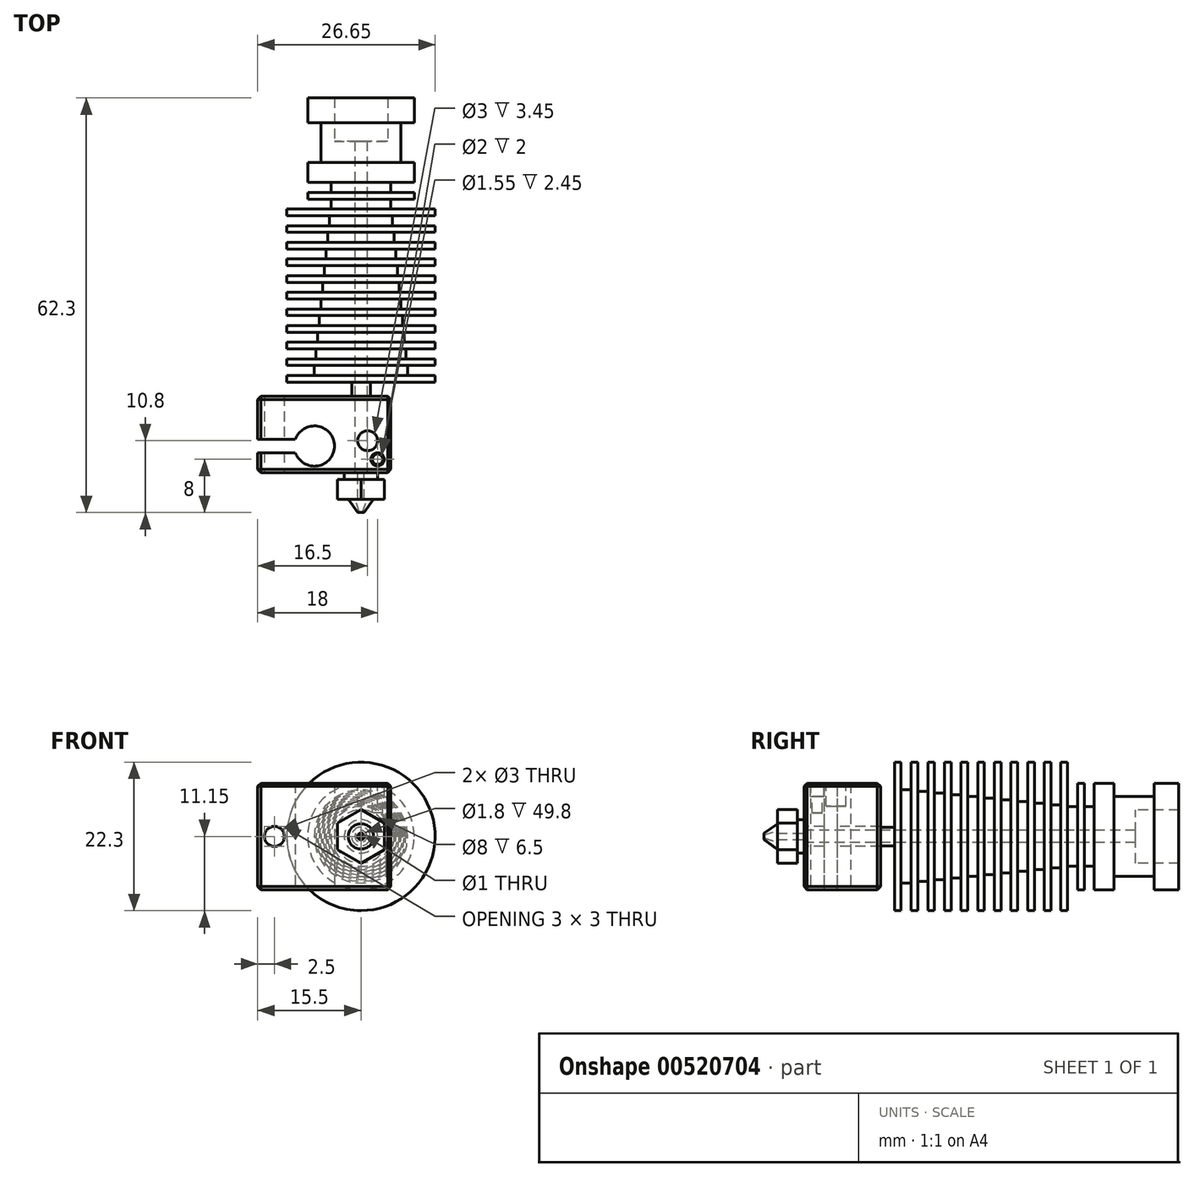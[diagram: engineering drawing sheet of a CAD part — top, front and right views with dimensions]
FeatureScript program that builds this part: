
annotation { "Feature Type Name" : "Feature", "Feature Type Description" : "" }
export const myFeature = defineFeature(function(context is Context, id is Id, definition is map)
    precondition{}
    {
        {
            var Q0;
            Q0=qCreatedBy(makeId("Top.planeOp"),FACE);
            var sketch = newSketch(context, id + "F0", { "sketchPlane" : qUnion([Q0])});
            skLineSegment(sketch, "E0", {"start": v(-8, 21.35) * mm, "end": v(-0.9, 21.35) * mm, "construction": true});
            skLineSegment(sketch, "E1", {"start": v(-0.9, 21.35) * mm, "end": v(-0.9, -38.95) * mm});
            skLineSegment(sketch, "E2", {"start": v(-0.9, 21.35) * mm, "end": v(-8, 21.35) * mm});
            skLineSegment(sketch, "E3", {"start": v(-6, 17.65) * mm, "end": v(-6, 11.65) * mm});
            skLineSegment(sketch, "E4", {"start": v(-8, 17.65) * mm, "end": v(-6, 17.65) * mm});
            skLineSegment(sketch, "E5", {"start": v(-8, 17.65) * mm, "end": v(-8, 21.35) * mm});
            skLineSegment(sketch, "E6", {"start": v(-8, 11.65) * mm, "end": v(-6, 11.65) * mm});
            skLineSegment(sketch, "E7", {"start": v(-8, 11.65) * mm, "end": v(-8, 8.65) * mm});
            skLineSegment(sketch, "E8", {"start": v(-8, 8.65) * mm, "end": v(-4.5, 8.65) * mm});
            skLineSegment(sketch, "E9", {"start": v(-4.5, 8.65) * mm, "end": v(-4.5, 7.15) * mm});
            skLineSegment(sketch, "E10", {"start": v(-4.5, 7.15) * mm, "end": v(-8, 7.15) * mm});
            skLineSegment(sketch, "E11", {"start": v(-8, 7.15) * mm, "end": v(-8, 6.15) * mm});
            skLineSegment(sketch, "E12", {"start": v(-8, 6.15) * mm, "end": v(-4.5, 6.15) * mm});
            skLineSegment(sketch, "E13", {"start": v(-4.5, 6.15) * mm, "end": v(-4.5, 4.65) * mm});
            skLineSegment(sketch, "E14", {"start": v(-4.5, 4.65) * mm, "end": v(-11.15, 4.65) * mm});
            skLineSegment(sketch, "E15", {"start": v(-11.15, 4.65) * mm, "end": v(-11.15, 3.65) * mm});
            skLineSegment(sketch, "E16", {"start": v(-11.15, 3.65) * mm, "end": v(-4.75, 3.65) * mm});
            skLineSegment(sketch, "E17", {"start": v(-4.75, 3.65) * mm, "end": v(-4.75, 2.15) * mm});
            skLineSegment(sketch, "E18", {"start": v(-4.75, 2.15) * mm, "end": v(-11.15, 2.15) * mm});
            skLineSegment(sketch, "E19", {"start": v(-11.15, 2.15) * mm, "end": v(-11.15, 1.15) * mm});
            skLineSegment(sketch, "E20", {"start": v(-11.15, 1.15) * mm, "end": v(-5, 1.15) * mm});
            skLineSegment(sketch, "E21", {"start": v(-5, 1.15) * mm, "end": v(-5, -0.35) * mm});
            skLineSegment(sketch, "E22", {"start": v(-5, -0.35) * mm, "end": v(-11.15, -0.35) * mm});
            skLineSegment(sketch, "E23", {"start": v(-11.15, -0.35) * mm, "end": v(-11.15, -1.35) * mm});
            skLineSegment(sketch, "E24", {"start": v(-11.15, -1.35) * mm, "end": v(-5.25, -1.35) * mm});
            skLineSegment(sketch, "E25", {"start": v(-5.25, -1.35) * mm, "end": v(-5.25, -2.85) * mm});
            skLineSegment(sketch, "E26", {"start": v(-5.25, -2.85) * mm, "end": v(-11.15, -2.85) * mm});
            skLineSegment(sketch, "E27", {"start": v(-11.15, -2.85) * mm, "end": v(-11.15, -3.85) * mm});
            skLineSegment(sketch, "E28", {"start": v(-11.15, -3.85) * mm, "end": v(-5.5, -3.85) * mm});
            skLineSegment(sketch, "E29", {"start": v(-5.5, -3.85) * mm, "end": v(-5.5, -5.35) * mm});
            skLineSegment(sketch, "E30", {"start": v(-5.5, -5.35) * mm, "end": v(-11.15, -5.35) * mm});
            skLineSegment(sketch, "E31", {"start": v(-11.15, -5.35) * mm, "end": v(-11.15, -6.35) * mm});
            skLineSegment(sketch, "E32", {"start": v(-11.15, -6.35) * mm, "end": v(-5.75, -6.35) * mm});
            skLineSegment(sketch, "E33", {"start": v(-5.75, -6.35) * mm, "end": v(-5.75, -7.85) * mm});
            skLineSegment(sketch, "E34", {"start": v(-5.75, -7.85) * mm, "end": v(-11.15, -7.85) * mm});
            skLineSegment(sketch, "E35", {"start": v(-11.15, -7.85) * mm, "end": v(-11.15, -8.85) * mm});
            skLineSegment(sketch, "E36", {"start": v(-11.15, -8.85) * mm, "end": v(-6, -8.85) * mm});
            skLineSegment(sketch, "E37", {"start": v(-6, -8.85) * mm, "end": v(-6, -10.35) * mm});
            skLineSegment(sketch, "E38", {"start": v(-6, -10.35) * mm, "end": v(-11.15, -10.35) * mm});
            skLineSegment(sketch, "E39", {"start": v(-11.15, -10.35) * mm, "end": v(-11.15, -11.35) * mm});
            skLineSegment(sketch, "E40", {"start": v(-11.15, -11.35) * mm, "end": v(-6.25, -11.35) * mm});
            skLineSegment(sketch, "E41", {"start": v(-6.25, -11.35) * mm, "end": v(-6.25, -12.85) * mm});
            skLineSegment(sketch, "E42", {"start": v(-6.25, -12.85) * mm, "end": v(-11.15, -12.85) * mm});
            skLineSegment(sketch, "E43", {"start": v(-11.15, -12.85) * mm, "end": v(-11.15, -13.85) * mm});
            skLineSegment(sketch, "E44", {"start": v(-11.15, -13.85) * mm, "end": v(-6.5, -13.85) * mm});
            skLineSegment(sketch, "E45", {"start": v(-6.5, -13.85) * mm, "end": v(-6.5, -15.35) * mm});
            skLineSegment(sketch, "E46", {"start": v(-6.5, -15.35) * mm, "end": v(-11.15, -15.35) * mm});
            skLineSegment(sketch, "E47", {"start": v(-11.15, -15.35) * mm, "end": v(-11.15, -16.35) * mm});
            skLineSegment(sketch, "E48", {"start": v(-11.15, -16.35) * mm, "end": v(-6.75, -16.35) * mm});
            skLineSegment(sketch, "E49", {"start": v(-6.75, -16.35) * mm, "end": v(-6.75, -17.85) * mm});
            skLineSegment(sketch, "E50", {"start": v(-6.75, -17.85) * mm, "end": v(-11.15, -17.85) * mm});
            skLineSegment(sketch, "E51", {"start": v(-11.15, -17.85) * mm, "end": v(-11.15, -18.85) * mm});
            skLineSegment(sketch, "E52", {"start": v(-11.15, -18.85) * mm, "end": v(-7, -18.85) * mm});
            skLineSegment(sketch, "E53", {"start": v(-7, -18.85) * mm, "end": v(-7, -20.35) * mm});
            skLineSegment(sketch, "E54", {"start": v(-7, -20.35) * mm, "end": v(-11.15, -20.35) * mm});
            skLineSegment(sketch, "E55", {"start": v(-11.15, -20.35) * mm, "end": v(-11.15, -21.35) * mm});
            skLineSegment(sketch, "E56", {"start": v(-11.15, -21.35) * mm, "end": v(-1.4, -21.35) * mm});
            skLineSegment(sketch, "E57", {"start": v(-1.4, -21.35) * mm, "end": v(-1.4, -23.45) * mm});
            skLineSegment(sketch, "E58", {"start": v(-1.4, -23.45) * mm, "end": v(-1.4, -34.95) * mm});
            skLineSegment(sketch, "E59", {"start": v(-1.4, -34.95) * mm, "end": v(-2.5, -34.95) * mm});
            skLineSegment(sketch, "E60", {"start": v(-2.5, -34.95) * mm, "end": v(-2.5, -35.95) * mm});
            skLineSegment(sketch, "E61", {"start": v(-0.2, -40.95) * mm, "end": v(-0.9, -38.95) * mm});
            skLineSegment(sketch, "E62", {"start": v(-0.2, -40.95) * mm, "end": v(-0.5, -40.95) * mm});
            skLineSegment(sketch, "E63", {"start": v(-0.5, -40.95) * mm, "end": v(-1.9, -38.95) * mm});
            skLineSegment(sketch, "E64", {"start": v(-1.9, -38.95) * mm, "end": v(-2.5, -35.95) * mm});
            skLineSegment(sketch, "E65", {"start": v(0, 0) * mm, "end": v(0, 30) * mm, "construction": true});
            skLineSegment(sketch, "E66", {"start": v(-1.4, -23.45) * mm, "end": v(-15.5, -23.45) * mm});
            skLineSegment(sketch, "E67", {"start": v(-15.5, -23.45) * mm, "end": v(-15.5, -34.95) * mm});
            skLineSegment(sketch, "E68", {"start": v(-15.5, -34.95) * mm, "end": v(4.5, -34.95) * mm});
            skLineSegment(sketch, "E69", {"start": v(4.5, -34.95) * mm, "end": v(4.5, -23.45) * mm});
            skLineSegment(sketch, "E70", {"start": v(4.5, -23.45) * mm, "end": v(-1.4, -23.45) * mm});
            skLineSegment(sketch, "E71", {"start": v(-15.5, -29.95) * mm, "end": v(-9.85, -29.95) * mm});
            skLineSegment(sketch, "E72", {"start": v(-15.5, -31.95) * mm, "end": v(-9.85, -31.95) * mm});
            skArc(sketch, "E73", {"start": v(-9.85, -31.95) * mm, "mid": v(-3.97, -30.95) * mm, "end": v(-9.85, -29.95) * mm});
            skLineSegment(sketch, "E74", {"start": v(0, -23.45) * mm, "end": v(0, -34.95) * mm});
            skLineSegment(sketch, "E75", {"start": v(-4, 21.35) * mm, "end": v(-4, 14.85) * mm});
            skLineSegment(sketch, "E76", {"start": v(-4, 14.85) * mm, "end": v(-0.9, 14.85) * mm});
            skSolve(sketch);
        }
        {
            var Q0;
            {var subQ6=sQuery(id+"F0.wireOp",EDGE,"E58");Q0=makeQuery(id+"F0.imprint","IMPRINT",FACE,{"disambiguationData":[TD([[makeQuery(id+"F0.imprint","IMPRINT",EDGE,{"derivedFrom":subQ6}),-1.0]])]});}
            var Q1;
            {var subQ5=sQuery(id+"F0.wireOp",EDGE,"E69");Q1=makeQuery(id+"F0.imprint","IMPRINT",FACE,{"disambiguationData":[TD([[makeQuery(id+"F0.imprint","IMPRINT",EDGE,{"derivedFrom":subQ5}),1.0]])]});}
            var Q2;
            {var subQ5=sQuery(id+"F0.wireOp",EDGE,"E58");Q2=makeQuery(id+"F0.imprint","IMPRINT",FACE,{"disambiguationData":[TD([[makeQuery(id+"F0.imprint","IMPRINT",EDGE,{"derivedFrom":subQ5}),1.0]])]});}
            var Q3;
            {var subQ5=sQuery(id+"F0.wireOp",EDGE,"E74");Q3=makeQuery(id+"F0.imprint","IMPRINT",FACE,{"disambiguationData":[TD([[makeQuery(id+"F0.imprint","IMPRINT",EDGE,{"derivedFrom":subQ5}),-1.0]])]});}
            extrude(context, id + "F1", {"entities" : qUnion([Q0, Q1, Q2, Q3]), "depth" : 8 * mm, "offsetDistance" : 25 * mm, "hasSecondDirection" : true, "secondDirectionOppositeDirection" : true, "secondDirectionDepth" : 8 * mm});
        }
        {
            var Q0;
            {var subQ5=sQuery(id+"F0.wireOp",EDGE,"E58");Q0=makeQuery(id+"F0.imprint","IMPRINT",FACE,{"disambiguationData":[TD([[makeQuery(id+"F0.imprint","IMPRINT",EDGE,{"derivedFrom":subQ5}),1.0]])]});}
            var Q1;
            {var subQ0=sQuery(id+"F0.wireOp",EDGE,"E60");Q1=makeQuery(id+"F0.imprint","IMPRINT",FACE,{"disambiguationData":[TD([[makeQuery(id+"F0.imprint","IMPRINT",EDGE,{"derivedFrom":subQ0}),1.0]])]});}
            var Q2;
            Q2=makeQuery(id+"F0.imprint","IMPRINT",FACE,{"disambiguationData":[TD([[makeQuery(id+"F0.imprint","IMPRINT",EDGE,{"derivedFrom":sQuery(id+"F0.wireOp",EDGE,"E3")}),1.0]])]});
            var Q3;
            Q3=sQuery(id+"F0.wireOp",EDGE,"E65");
            revolve(context, id + "F2", {"operationType" : NewBodyOperationType.ADD, "entities" : qUnion([Q0, Q1, Q2]), "axis" : qUnion([Q3]), "revolveType" : RevolveType.FULL});
        }
        {
            var Q0;
            {var subQ5=sQuery(id+"F0.wireOp",EDGE,"E74");Q0=makeQuery(id+"F0.imprint","IMPRINT",FACE,{"disambiguationData":[TD([[makeQuery(id+"F0.imprint","IMPRINT",EDGE,{"derivedFrom":subQ5}),-1.0]])]});}
            var Q1;
            Q1=sQuery(id+"F0.wireOp",EDGE,"E65");
            revolve(context, id + "F3", {"operationType" : NewBodyOperationType.REMOVE, "entities" : qUnion([Q0]), "axis" : qUnion([Q1]), "revolveType" : RevolveType.FULL, "oppositeDirection" : true});
        }
        {
            var Q0;
            Q0=makeQuery(id+"F1.opExtrude","SWEPT_EDGE",EDGE,{"disambiguationData":[OSD([sQuery(id+"F0.wireOp",EDGE,"E66"),sQuery(id+"F0.wireOp",EDGE,"E67")])]});
            var Q1;
            {var subQ0=sQuery(id+"F0.wireOp",EDGE,"E67");Q1=makeQuery(id+"F1.opExtrude","CAP_EDGE",EDGE,{"disambiguationData":[OSD([subQ0]),TDD([makeQuery(id+"F0.imprint","IMPRINT",EDGE,{"disambiguationData":[TD([[makeQuery(id+"F0.imprint","INTERSECT",VERTEX,{"derivedFrom":[sQuery(id+"F0.wireOp",EDGE,"E66"),subQ0]}),-1.0]])],"derivedFrom":subQ0})])],"isStart":false});}
            var Q2;
            Q2=makeQuery(id+"F1.opExtrude","CAP_EDGE",EDGE,{"disambiguationData":[OSD([sQuery(id+"F0.wireOp",EDGE,"E66"),sQuery(id+"F0.wireOp",EDGE,"E70")])],"isStart":false});
            var Q3;
            {var subQ0=sQuery(id+"F0.wireOp",EDGE,"E67");Q3=makeQuery(id+"F1.opExtrude","CAP_EDGE",EDGE,{"disambiguationData":[OSD([subQ0]),TDD([makeQuery(id+"F0.imprint","IMPRINT",EDGE,{"disambiguationData":[TD([[makeQuery(id+"F0.imprint","INTERSECT",VERTEX,{"derivedFrom":[sQuery(id+"F0.wireOp",EDGE,"E66"),subQ0]}),-1.0]])],"derivedFrom":subQ0})])],"isStart":true});}
            var Q4;
            {var subQ0=sQuery(id+"F0.wireOp",EDGE,"E67");Q4=makeQuery(id+"F1.opExtrude","CAP_EDGE",EDGE,{"disambiguationData":[OSD([subQ0]),TDD([makeQuery(id+"F0.imprint","IMPRINT",EDGE,{"disambiguationData":[TD([[makeQuery(id+"F0.imprint","INTERSECT",VERTEX,{"derivedFrom":[subQ0,sQuery(id+"F0.wireOp",EDGE,"E68")]}),1.0]])],"derivedFrom":subQ0})])],"isStart":true});}
            var Q5;
            {var subQ0=sQuery(id+"F0.wireOp",EDGE,"E67");Q5=makeQuery(id+"F1.opExtrude","CAP_EDGE",EDGE,{"disambiguationData":[OSD([subQ0]),TDD([makeQuery(id+"F0.imprint","IMPRINT",EDGE,{"disambiguationData":[TD([[makeQuery(id+"F0.imprint","INTERSECT",VERTEX,{"derivedFrom":[subQ0,sQuery(id+"F0.wireOp",EDGE,"E68")]}),1.0]])],"derivedFrom":subQ0})])],"isStart":false});}
            var Q6;
            Q6=makeQuery(id+"F1.opExtrude","CAP_EDGE",EDGE,{"disambiguationData":[OSD([sQuery(id+"F0.wireOp",EDGE,"E69")])],"isStart":true});
            var Q7;
            Q7=makeQuery(id+"F1.opExtrude","CAP_EDGE",EDGE,{"disambiguationData":[OSD([sQuery(id+"F0.wireOp",EDGE,"E66"),sQuery(id+"F0.wireOp",EDGE,"E70")])],"isStart":true});
            var Q8;
            Q8=makeQuery(id+"F1.opExtrude","CAP_EDGE",EDGE,{"disambiguationData":[OSD([sQuery(id+"F0.wireOp",EDGE,"E68")])],"isStart":true});
            var Q9;
            Q9=makeQuery(id+"F1.opExtrude","SWEPT_EDGE",EDGE,{"disambiguationData":[OSD([sQuery(id+"F0.wireOp",EDGE,"E67"),sQuery(id+"F0.wireOp",EDGE,"E68")])]});
            var Q10;
            Q10=makeQuery(id+"F1.opExtrude","SWEPT_EDGE",EDGE,{"disambiguationData":[OSD([sQuery(id+"F0.wireOp",EDGE,"E69"),sQuery(id+"F0.wireOp",EDGE,"E70")])]});
            var Q11;
            Q11=makeQuery(id+"F1.opExtrude","SWEPT_EDGE",EDGE,{"disambiguationData":[OSD([sQuery(id+"F0.wireOp",EDGE,"E68"),sQuery(id+"F0.wireOp",EDGE,"E69")])]});
            var Q12;
            Q12=makeQuery(id+"F1.opExtrude","CAP_EDGE",EDGE,{"disambiguationData":[OSD([sQuery(id+"F0.wireOp",EDGE,"E69")])],"isStart":false});
            var Q13;
            Q13=makeQuery(id+"F1.opExtrude","CAP_EDGE",EDGE,{"disambiguationData":[OSD([sQuery(id+"F0.wireOp",EDGE,"E68")])],"isStart":false});
            chamfer(context, id + "F4", {"entities" : qUnion([Q0, Q1, Q2, Q3, Q4, Q5, Q6, Q7, Q8, Q9, Q10, Q11, Q12, Q13]), "width" : 0.5 * mm, "tangentPropagation" : true});
        }
        {
            var Q0;
            Q0=makeQuery(id+"F1.opExtrude","CAP_FACE",FACE,{"disambiguationData":[OSD([sQuery(id+"F0.wireOp",EDGE,"E66"),sQuery(id+"F0.wireOp",EDGE,"E67"),sQuery(id+"F0.wireOp",EDGE,"E68"),sQuery(id+"F0.wireOp",EDGE,"E69"),sQuery(id+"F0.wireOp",EDGE,"E70"),sQuery(id+"F0.wireOp",EDGE,"E71"),sQuery(id+"F0.wireOp",EDGE,"E72"),sQuery(id+"F0.wireOp",EDGE,"E73")])],"isStart":false});
            var sketch = newSketch(context, id + "F5", { "sketchPlane" : qUnion([Q0])});
            skCircle(sketch, "E77", {"center": v(1, -30.15) * mm, "radius": 1.5 * mm});
            skPoint(sketch, "E77.first.point", {"position": v(1.08, -28.65) * mm});
            skPoint(sketch, "E77.second.point", {"position": v(-0.28, -30.93) * mm});
            skPoint(sketch, "E77.third.point", {"position": v(2.31, -30.88) * mm});
            skCircle(sketch, "E78", {"center": v(2.5, -32.95) * mm, "radius": 1 * mm});
            skPoint(sketch, "E78.first.point", {"position": v(2.5, -31.95) * mm});
            skPoint(sketch, "E78.second.point", {"position": v(1.79, -33.65) * mm});
            skPoint(sketch, "E78.third.point", {"position": v(3.26, -33.6) * mm});
            skCircle(sketch, "E79", {"center": v(2.5, -32.95) * mm, "radius": 0.78 * mm});
            skSolve(sketch);
        }
        {
            var Q0;
            Q0=makeQuery(id+"F5.imprint","IMPRINT",FACE,{"disambiguationData":[TD([[makeQuery(id+"F5.imprint","IMPRINT",EDGE,{"derivedFrom":sQuery(id+"F5.wireOp",EDGE,"E77")}),1.0]])]});
            extrude(context, id + "F6", {"entities" : qUnion([Q0]), "operationType" : NewBodyOperationType.REMOVE, "oppositeDirection" : true, "depth" : 3.45 * mm, "offsetDistance" : 25 * mm});
        }
        {
            var Q0;
            Q0=makeQuery(id+"F5.imprint","IMPRINT",FACE,{"disambiguationData":[TD([[makeQuery(id+"F5.imprint","IMPRINT",EDGE,{"derivedFrom":sQuery(id+"F5.wireOp",EDGE,"E79")}),1.0]])]});
            extrude(context, id + "F7", {"entities" : qUnion([Q0]), "operationType" : NewBodyOperationType.REMOVE, "oppositeDirection" : true, "depth" : 4.45 * mm, "offsetDistance" : 25 * mm});
        }
        {
            var Q0;
            Q0=makeQuery(id+"F5.imprint","IMPRINT",FACE,{"disambiguationData":[TD([[makeQuery(id+"F5.imprint","IMPRINT",EDGE,{"derivedFrom":sQuery(id+"F5.wireOp",EDGE,"E78")}),1.0]])]});
            extrude(context, id + "F8", {"entities" : qUnion([Q0]), "operationType" : NewBodyOperationType.REMOVE, "oppositeDirection" : true, "depth" : 2 * mm, "offsetDistance" : 25 * mm});
        }
        {
            var Q0;
            {var subQ0=sQuery(id+"F0.wireOp",EDGE,"E68");var subQ3=sQuery(id+"F0.wireOp",EDGE,"E69");Q0=makeQuery(id+"F2.boolean.opBoolean","SPLIT",FACE,{"disambiguationData":[TD([makeQuery(id+"F1.opExtrude","SWEPT_FACE",FACE,{"disambiguationData":[OSD([subQ3])]})])],"derivedFrom":makeQuery(id+"F1.opExtrude","SWEPT_FACE",FACE,{"disambiguationData":[OSD([subQ0])]})});}
            var sketch = newSketch(context, id + "F9", { "sketchPlane" : qUnion([Q0])});
            skCircle(sketch, "E80", {"center": v(-13, 0) * mm, "radius": 1.5 * mm});
            skPoint(sketch, "E80.first.point", {"position": v(-13, 1.5) * mm});
            skPoint(sketch, "E80.second.point", {"position": v(-13.86, -1.23) * mm});
            skPoint(sketch, "E80.third.point", {"position": v(-11.72, -0.78) * mm});
            skCircle(sketch, "E81.cCircle", {"center": v(0, 0) * mm, "radius": 3.5 * mm, "construction": true});
            skLineSegment(sketch, "E81.0", {"start": v(3.5, 2.02) * mm, "end": v(3.5, -2.02) * mm});
            skLineSegment(sketch, "E81.1", {"start": v(3.5, -2.02) * mm, "end": v(0, -4.04) * mm});
            skLineSegment(sketch, "E81.2", {"start": v(0, -4.04) * mm, "end": v(-3.5, -2.02) * mm});
            skLineSegment(sketch, "E81.3", {"start": v(-3.5, -2.02) * mm, "end": v(-3.5, 2.02) * mm});
            skLineSegment(sketch, "E81.4", {"start": v(-3.5, 2.02) * mm, "end": v(0, 4.04) * mm});
            skLineSegment(sketch, "E81.5", {"start": v(0, 4.04) * mm, "end": v(3.5, 2.02) * mm});
            skPoint(sketch, "E81.0.midPoint", {"position": v(3.5, 0) * mm});
            skCircle(sketch, "E82", {"center": v(0, 0) * mm, "radius": 0.5 * mm});
            skSolve(sketch);
        }
        {
            var Q0;
            Q0=makeQuery(id+"F9.imprint","IMPRINT",FACE,{"disambiguationData":[TD([[makeQuery(id+"F9.imprint","IMPRINT",EDGE,{"derivedFrom":sQuery(id+"F9.wireOp",EDGE,"E80")}),1.0]])]});
            extrude(context, id + "F10", {"entities" : qUnion([Q0]), "operationType" : NewBodyOperationType.REMOVE, "oppositeDirection" : true, "depth" : 11.6 * mm, "offsetDistance" : 25 * mm});
        }
        {
            var Q0;
            Q0=makeQuery(id+"F9.imprint","IMPRINT",FACE,{"disambiguationData":[TD([[makeQuery(id+"F9.imprint","IMPRINT",EDGE,{"derivedFrom":sQuery(id+"F9.wireOp",EDGE,"E82")}),-1.0]])]});
            var Q1;
            Q1=makeQuery(id+"F9.imprint","IMPRINT",FACE,{"disambiguationData":[TD([[makeQuery(id+"F9.imprint","IMPRINT",EDGE,{"derivedFrom":sQuery(id+"F9.wireOp",EDGE,"E81.0")}),-1.0]])]});
            extrude(context, id + "F11", {"entities" : qUnion([Q0, Q1]), "operationType" : NewBodyOperationType.ADD, "depth" : 4 * mm, "offsetDistance" : 25 * mm});
        }
        {
            var Q0;
            Q0=makeQuery(id+"F9.imprint","IMPRINT",FACE,{"disambiguationData":[TD([[makeQuery(id+"F9.imprint","IMPRINT",EDGE,{"derivedFrom":sQuery(id+"F9.wireOp",EDGE,"E81.0")}),-1.0]])]});
            extrude(context, id + "F12", {"entities" : qUnion([Q0]), "operationType" : NewBodyOperationType.REMOVE, "depth" : 1 * mm, "offsetDistance" : 25 * mm});
        }
    });
